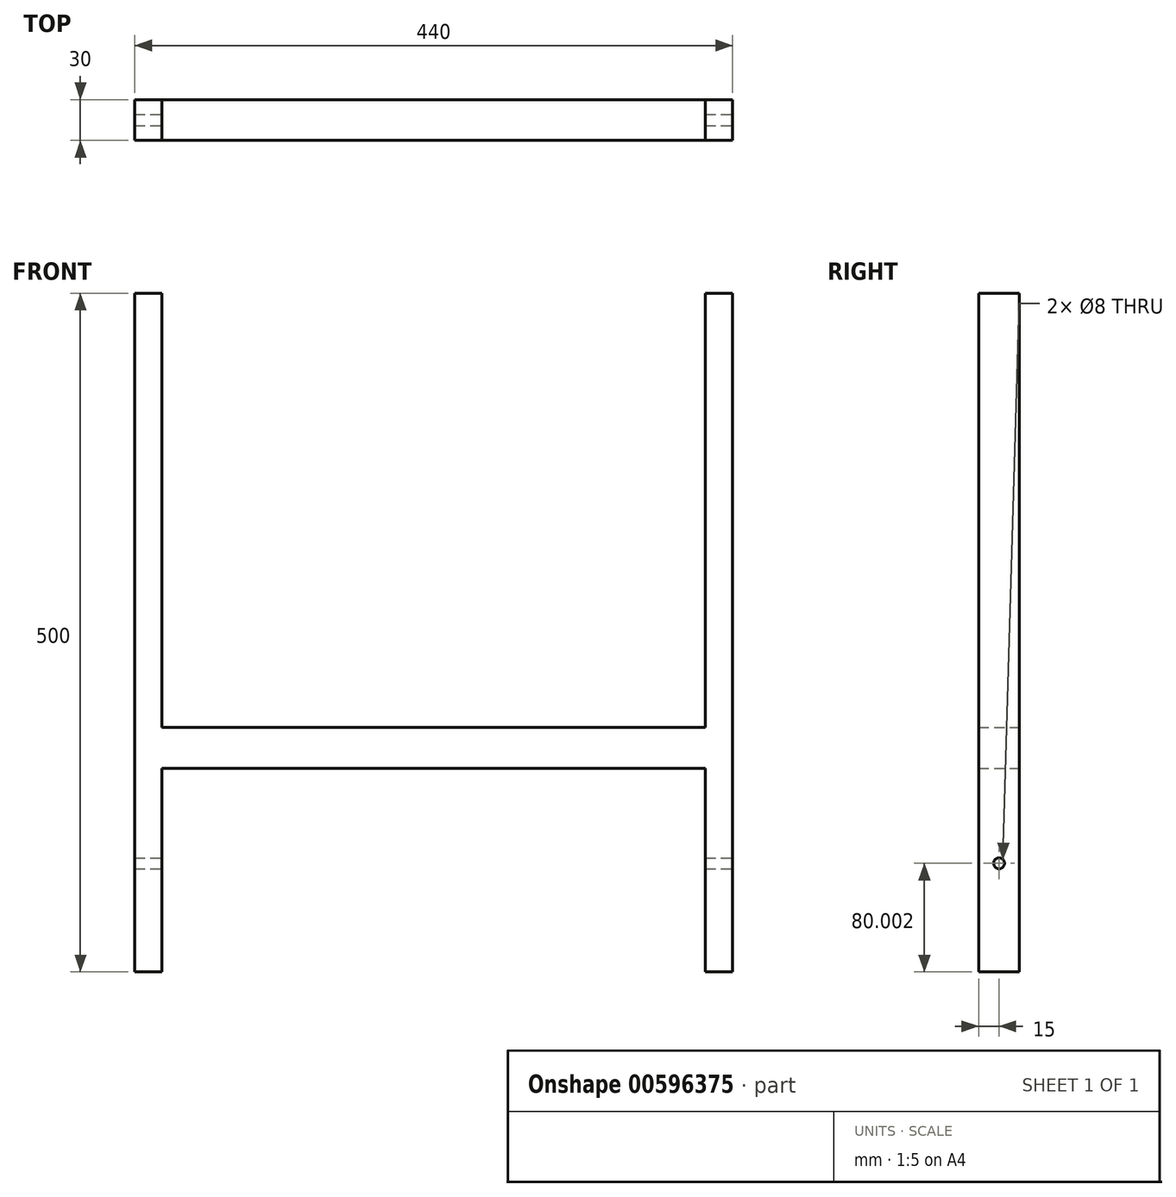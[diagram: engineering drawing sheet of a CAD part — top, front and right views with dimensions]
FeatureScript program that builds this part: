
annotation { "Feature Type Name" : "Feature", "Feature Type Description" : "" }
export const myFeature = defineFeature(function(context is Context, id is Id, definition is map)
    precondition{}
    {
        {
            var Q0;
            Q0=qCreatedBy(makeId("Front.planeOp"),FACE);
            var sketch = newSketch(context, id + "F0", { "sketchPlane" : qUnion([Q0])});
            skLineSegment(sketch, "E0.bottom", {"start": v(-270, 151.06) * mm, "end": v(-250, 151.06) * mm});
            skLineSegment(sketch, "E0.top", {"start": v(-270, -348.94) * mm, "end": v(-250, -348.94) * mm});
            skLineSegment(sketch, "E0.left", {"start": v(-270, 151.06) * mm, "end": v(-270, -348.94) * mm});
            skLineSegment(sketch, "E0.right", {"start": v(-250, 151.06) * mm, "end": v(-250, -348.94) * mm});
            skLineSegment(sketch, "E1.bottom", {"start": v(150, 151.06) * mm, "end": v(170, 151.06) * mm});
            skLineSegment(sketch, "E1.top", {"start": v(150, -348.94) * mm, "end": v(170, -348.94) * mm});
            skLineSegment(sketch, "E1.left", {"start": v(150, 151.06) * mm, "end": v(150, -348.94) * mm});
            skLineSegment(sketch, "E1.right", {"start": v(170, 151.06) * mm, "end": v(170, -348.94) * mm});
            skLineSegment(sketch, "E2.bottom", {"start": v(-250, -168.94) * mm, "end": v(150, -168.94) * mm});
            skLineSegment(sketch, "E2.top", {"start": v(-250, -198.94) * mm, "end": v(150, -198.94) * mm});
            skLineSegment(sketch, "E2.left", {"start": v(-250, -168.94) * mm, "end": v(-250, -198.94) * mm});
            skLineSegment(sketch, "E2.right", {"start": v(150, -168.94) * mm, "end": v(150, -198.94) * mm});
            skSolve(sketch);
        }
        {
            var Q0;
            Q0 = qSketchRegion(id + "F0", true);
            extrude(context, id + "F1", {"entities" : qUnion([Q0]), "depth" : 30 * mm, "offsetDistance" : 25 * mm});
        }
        {
            var Q0;
            Q0=makeQuery(id+"F1.opExtrude","SWEPT_FACE",FACE,{"disambiguationData":[OSD([sQuery(id+"F0.wireOp",EDGE,"E1.right")])]});
            var sketch = newSketch(context, id + "F2", { "sketchPlane" : qUnion([Q0])});
            skCircle(sketch, "E3", {"center": v(-15, -268.94) * mm, "radius": 4 * mm});
            skLineSegment(sketch, "E4", {"start": v(-30, -268.94) * mm, "end": v(0, -268.94) * mm, "construction": true});
            skSolve(sketch);
        }
        {
            var Q0;
            Q0 = qSketchRegion(id + "F2", true);
            extrude(context, id + "F3", {"entities" : qUnion([Q0]), "operationType" : NewBodyOperationType.REMOVE, "endBound" : BoundingType.THROUGH_ALL, "oppositeDirection" : true, "depth" : 25 * mm, "offsetDistance" : 25 * mm});
        }
    });
